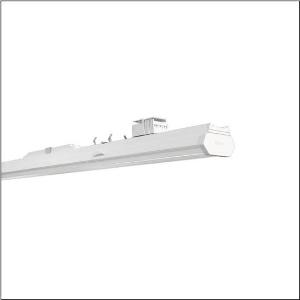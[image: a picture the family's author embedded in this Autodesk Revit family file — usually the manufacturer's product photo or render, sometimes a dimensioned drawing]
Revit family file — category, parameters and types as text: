
# Revit family: licross_r__11_protected_ho_51td13cn4e5s_07e4
name_source: partatom
category: Lighting Fixtures
units: mm (PartAtom-declared; Revit-internal decimal feet)

## family parameters
Cut with Voids When Loaded = No
Host = Face
Light Source = No
Part Type = Normal
Room Calculation Point = No
Round Connector Dimension = Use Diameter
Shared = No

## types (1)
- --- (1 x LED, 14500 lm, 77.6 W, 4000K)
    Apparent Load = 78 VA
    CIE Flux Codes = 89 96 99 100 99
    Color Rendering = 80
    Color Temperature = 4000K
    Default Elevation = 1800 mm
    Description = Licross® 11 Protected HO, luminaire insert, of sheet steel, galvanised, coil coated, white, length: 1.500mm, width: 90mm, height: 101mm, LED rated luminous flux: 14.500lm, light colour: 840, SDCM (Standard Deviation of Colour Matching)MacAdam ≤ 2 SDCM (initial), control gear: ON/OFF Multilumen, CLOi, with plug, 3-pole, with phase selection, mains connection: 220..240V, AC, 50/60Hz, start of lifetime: 78W, end of service life: 87W, internal wiring halogen-free, primary light control with lens, of plastic, primary optical cover: cover, of PMMA, light emission: direct distribution, primary light characteristic: symmetric, protection rating (complete): IP54, insulation class (complete): insulation class I (protective earthing), certification: CE, ENEC, VDE, UKCA, protection symbol: D if used in an environment with non-conductive dust loads with corresponding accessories, impact resistance: IK06, permissible ambient temperature for indoor applications: -35..+35°C, corresponds to IFS (International Featured Standards) requirements for safety and quality in the food industry, reducing of maximum allowable ambient temperature of 5°C with ceiling mounting, LABS conformity tested according to VDMA 24364:2018-05, packaging unit: 1 piece
    Height = 92 mm
    Lamp = 1 x LED
    Lamp Light Flux = 14500 lm
    Lamp Power = 77.6 W
    Lamp count = 1
    Length = 1500 mm
    Luminous efficacy = 187 lm/W
    Manufacturer = Siteco
    ModVariant = No
    Model = 51TD13CN4E5S
    Mounting Place = Ceiling
    Mounting Type = Pendant
    Number of Poles = 1
    OnlyDefault = Yes
    Power Factor = 1
    Product Name = Licross® 11 Protected HO
    Product group = luminaire insert | ceiling pendant
    ProductGroupID = 901
    Protection Class = Protection class I
    Protection Degree = IP 54
    RLX_Detail_Level = 1
    RLX_Emergency_Light_Flux = 0 lm
    RLX_Emergency_Type = 0
    RLX_Emergency_Type_DB = No
    RlxData = <blob elided: 22201 chars, md5=819936a5>
    Socket = socket
    Standby Power = 0 W
    System Light Flux = 14500 lm
    System Power = 78 W
    Type Comments = factory setting: luminous flux: 100 % | (A | C | E) | 181 mA
    Type Image = l_1256145.jpg
    URL = http://relux.com
    VarID = @adj_093415
    Voltage = 0 V
    Weight = 0.00 kg
    Width = 88 mm

## geometry (parser evidence)
native form markers: Blend x4, Sweep x13
no freeform markers — native parametric forms only
